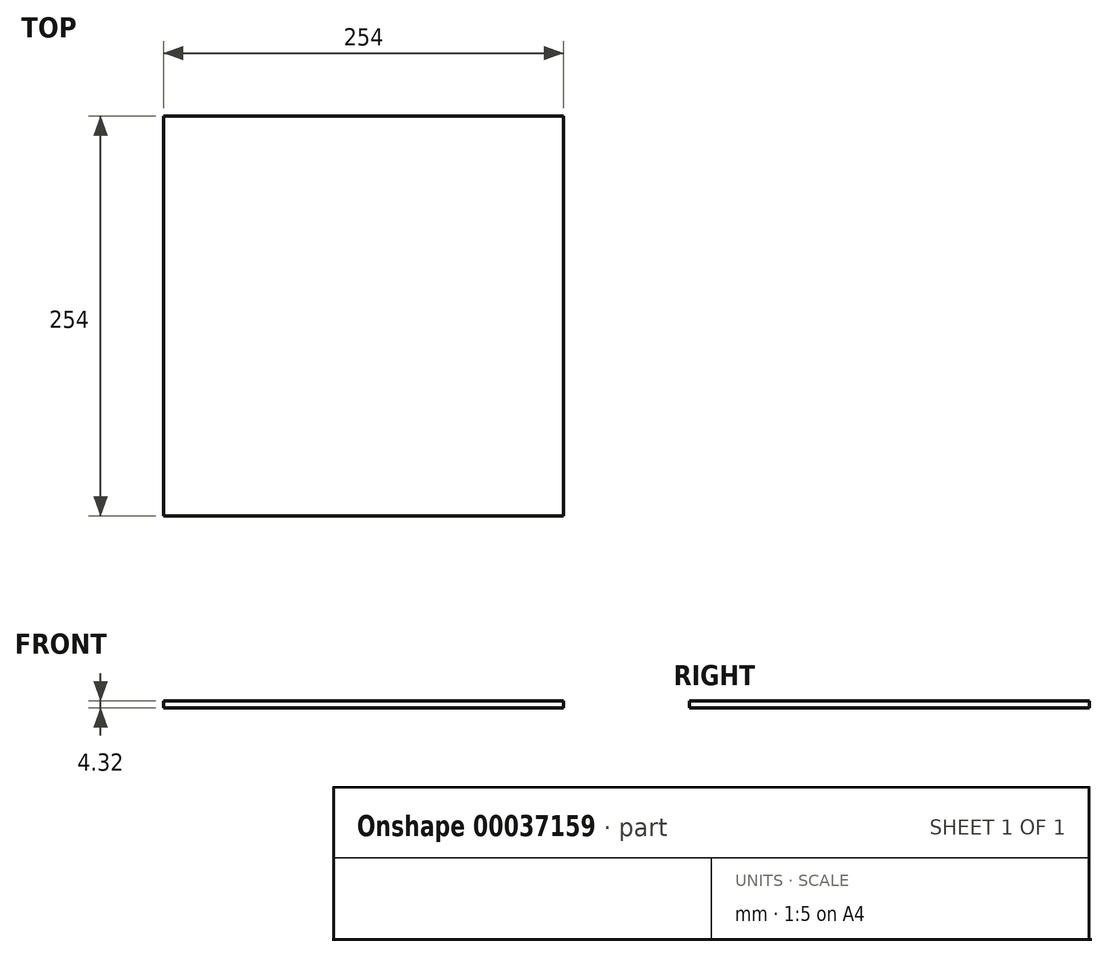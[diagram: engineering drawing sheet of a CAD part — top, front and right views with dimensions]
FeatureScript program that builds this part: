
annotation { "Feature Type Name" : "Feature", "Feature Type Description" : "" }
export const myFeature = defineFeature(function(context is Context, id is Id, definition is map)
    precondition{}
    {
        {
            var Q0;
            Q0=qCreatedBy(makeId("Top.planeOp"),FACE);
            var sketch = newSketch(context, id + "F0", { "sketchPlane" : qUnion([Q0])});
            skLineSegment(sketch, "E0.bottom", {"start": v(-124.68, 176.12) * mm, "end": v(129.32, 176.12) * mm});
            skLineSegment(sketch, "E0.top", {"start": v(-124.68, -77.88) * mm, "end": v(129.32, -77.88) * mm});
            skLineSegment(sketch, "E0.left", {"start": v(-124.68, 176.12) * mm, "end": v(-124.68, -77.88) * mm});
            skLineSegment(sketch, "E0.right", {"start": v(129.32, 176.12) * mm, "end": v(129.32, -77.88) * mm});
            skSolve(sketch);
        }
        {
            var Q0;
            Q0=makeQuery(id+"F0.imprint","IMPRINT",FACE,{"disambiguationData":[TD([[makeQuery(id+"F0.imprint","IMPRINT",EDGE,{"derivedFrom":sQuery(id+"F0.wireOp",EDGE,"E0.bottom")}),-1.0]])]});
            extrude(context, id + "F1", {"entities" : qUnion([Q0]), "depth" : 4.32 * mm});
        }
    });
